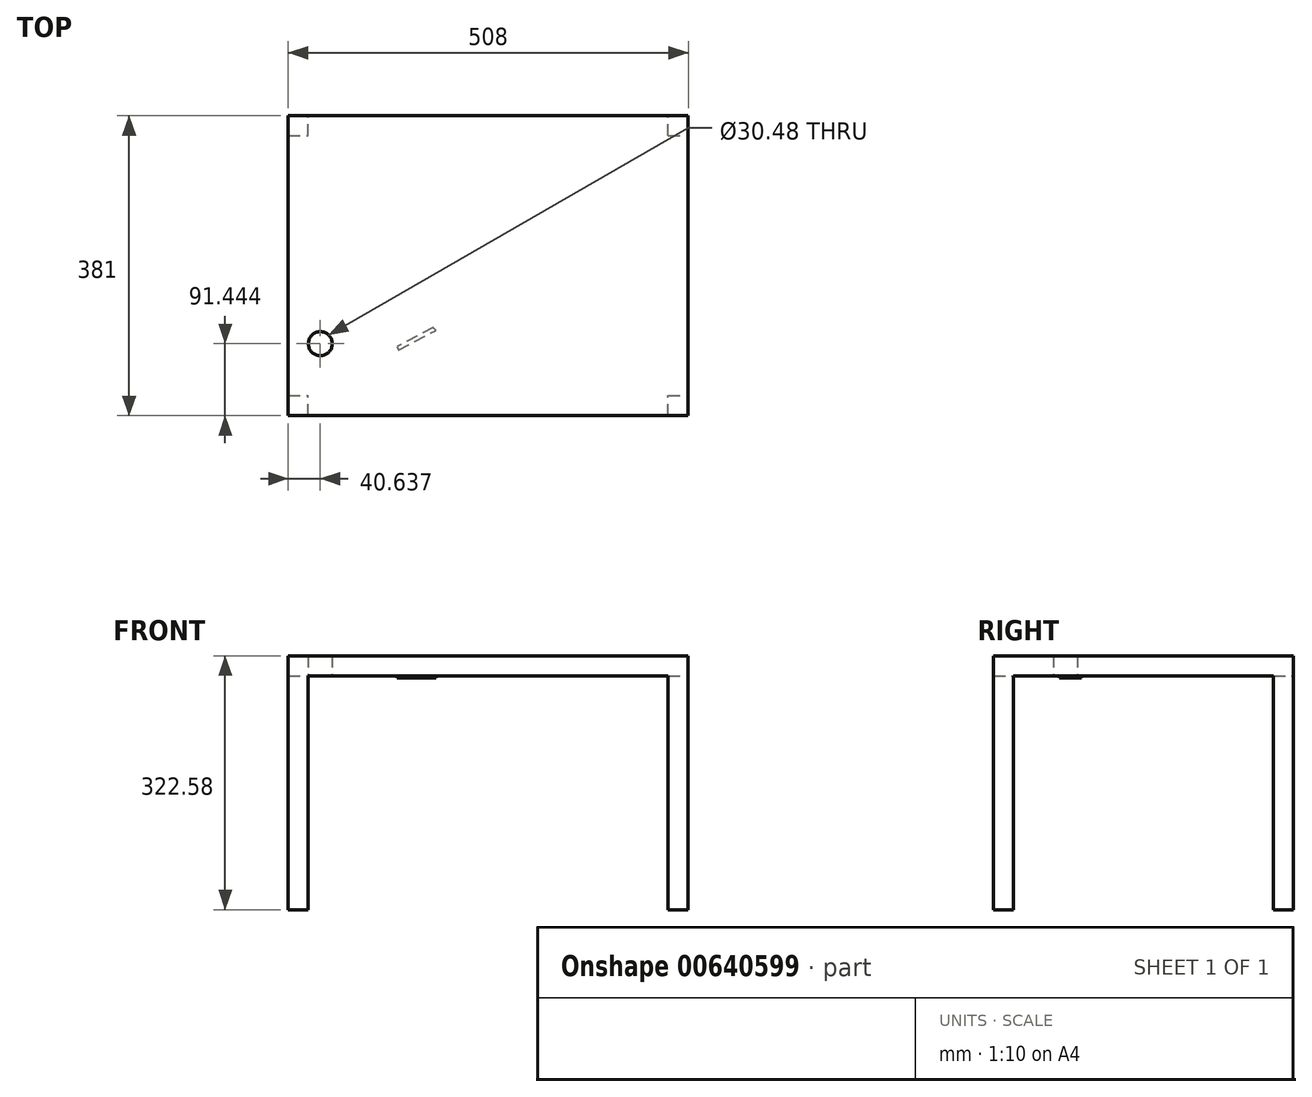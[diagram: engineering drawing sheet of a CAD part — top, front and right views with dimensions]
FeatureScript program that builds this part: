
annotation { "Feature Type Name" : "Feature", "Feature Type Description" : "" }
export const myFeature = defineFeature(function(context is Context, id is Id, definition is map)
    precondition{}
    {
        {
            var Q0;
            Q0=qCreatedBy(makeId("Top.planeOp"),FACE);
            var sketch = newSketch(context, id + "F0", { "sketchPlane" : qUnion([Q0])});
            skLineSegment(sketch, "E0.bottom", {"start": v(-266.43, 227.2) * mm, "end": v(241.57, 227.2) * mm});
            skLineSegment(sketch, "E0.top", {"start": v(-266.43, -153.8) * mm, "end": v(241.57, -153.8) * mm});
            skLineSegment(sketch, "E0.left", {"start": v(-266.43, 227.2) * mm, "end": v(-266.43, -153.8) * mm});
            skLineSegment(sketch, "E0.right", {"start": v(241.57, 227.2) * mm, "end": v(241.57, -153.8) * mm});
            skSolve(sketch);
        }
        {
            var Q0;
            Q0=makeQuery(id+"F0.imprint","IMPRINT",FACE,{"disambiguationData":[TD([[makeQuery(id+"F0.imprint","IMPRINT",EDGE,{"derivedFrom":sQuery(id+"F0.wireOp",EDGE,"E0.bottom")}),-1.0]])]});
            var sketch = newSketch(context, id + "F1", { "sketchPlane" : qUnion([Q0])});
            skSolve(sketch);
        }
        {
            var Q0;
            Q0=makeQuery(id+"F1.imprint","IMPRINT",FACE,{"disambiguationData":[TD([[makeQuery(id+"F1.imprint","IMPRINT",EDGE,{"derivedFrom":makeQuery(id+"F0.imprint","IMPRINT",EDGE,{"derivedFrom":sQuery(id+"F0.wireOp",EDGE,"E0.bottom")})}),-1.0]])]});
            var sketch = newSketch(context, id + "F2", { "sketchPlane" : qUnion([Q0])});
            skCircle(sketch, "E1", {"center": v(-225.8, -62.36) * mm, "radius": 15.24 * mm});
            skSolve(sketch);
        }
        {
            var Q0;
            Q0=makeQuery(id+"F2.imprint","IMPRINT",FACE,{"disambiguationData":[TD([[makeQuery(id+"F2.imprint","IMPRINT",EDGE,{"derivedFrom":sQuery(id+"F2.wireOp",EDGE,"E1")}),-1.0]])]});
            extrude(context, id + "F3", {"entities" : qUnion([Q0]), "depth" : 25.4 * mm, "offsetDistance" : 25.4 * mm});
        }
        {
            var Q0;
            Q0=makeQuery(id+"F0.imprint","IMPRINT",FACE,{"disambiguationData":[TD([[makeQuery(id+"F0.imprint","IMPRINT",EDGE,{"derivedFrom":sQuery(id+"F0.wireOp",EDGE,"E0.bottom")}),-1.0]])]});
            var sketch = newSketch(context, id + "F4", { "sketchPlane" : qUnion([Q0])});
            skLineSegment(sketch, "E2.bottom", {"start": v(-266.43, -153.8) * mm, "end": v(-241.03, -153.8) * mm});
            skLineSegment(sketch, "E2.top", {"start": v(-266.43, -128.4) * mm, "end": v(-241.03, -128.4) * mm});
            skLineSegment(sketch, "E2.left", {"start": v(-266.43, -153.8) * mm, "end": v(-266.43, -128.4) * mm});
            skLineSegment(sketch, "E2.right", {"start": v(-241.03, -153.8) * mm, "end": v(-241.03, -128.4) * mm});
            skLineSegment(sketch, "E3.bottom", {"start": v(-266.43, 201.8) * mm, "end": v(-241.03, 201.8) * mm});
            skLineSegment(sketch, "E3.top", {"start": v(-266.43, 227.2) * mm, "end": v(-241.03, 227.2) * mm});
            skLineSegment(sketch, "E3.left", {"start": v(-266.43, 201.8) * mm, "end": v(-266.43, 227.2) * mm});
            skLineSegment(sketch, "E3.right", {"start": v(-241.03, 201.8) * mm, "end": v(-241.03, 227.2) * mm});
            skLineSegment(sketch, "E4.bottom", {"start": v(216.17, -153.8) * mm, "end": v(241.57, -153.8) * mm});
            skLineSegment(sketch, "E4.top", {"start": v(216.17, -128.4) * mm, "end": v(241.57, -128.4) * mm});
            skLineSegment(sketch, "E4.left", {"start": v(216.17, -153.8) * mm, "end": v(216.17, -128.4) * mm});
            skLineSegment(sketch, "E4.right", {"start": v(241.57, -153.8) * mm, "end": v(241.57, -128.4) * mm});
            skLineSegment(sketch, "E5.bottom", {"start": v(216.17, 201.8) * mm, "end": v(241.57, 201.8) * mm});
            skLineSegment(sketch, "E5.top", {"start": v(216.17, 227.2) * mm, "end": v(241.57, 227.2) * mm});
            skLineSegment(sketch, "E5.left", {"start": v(216.17, 201.8) * mm, "end": v(216.17, 227.2) * mm});
            skLineSegment(sketch, "E5.right", {"start": v(241.57, 201.8) * mm, "end": v(241.57, 227.2) * mm});
            skSolve(sketch);
        }
        {
            var Q0;
            Q0=makeQuery(id+"F4.imprint","IMPRINT",FACE,{"disambiguationData":[TD([[makeQuery(id+"F4.imprint","IMPRINT",EDGE,{"derivedFrom":sQuery(id+"F4.wireOp",EDGE,"E2.bottom")}),1.0]])]});
            var Q1;
            Q1=makeQuery(id+"F4.imprint","IMPRINT",FACE,{"disambiguationData":[TD([[makeQuery(id+"F4.imprint","IMPRINT",EDGE,{"derivedFrom":sQuery(id+"F4.wireOp",EDGE,"E5.bottom")}),1.0]])]});
            var Q2;
            Q2=makeQuery(id+"F4.imprint","IMPRINT",FACE,{"disambiguationData":[TD([[makeQuery(id+"F4.imprint","IMPRINT",EDGE,{"derivedFrom":sQuery(id+"F4.wireOp",EDGE,"E4.bottom")}),1.0]])]});
            var Q3;
            Q3=makeQuery(id+"F4.imprint","IMPRINT",FACE,{"disambiguationData":[TD([[makeQuery(id+"F4.imprint","IMPRINT",EDGE,{"derivedFrom":sQuery(id+"F4.wireOp",EDGE,"E3.bottom")}),1.0]])]});
            extrude(context, id + "F5", {"entities" : qUnion([Q0, Q1, Q2, Q3]), "operationType" : NewBodyOperationType.ADD, "oppositeDirection" : true, "depth" : 297.18 * mm, "offsetDistance" : 25.4 * mm});
        }
        {
            var Q0;
            Q0=makeQuery(id+"F0.imprint","IMPRINT",FACE,{"disambiguationData":[TD([[makeQuery(id+"F0.imprint","IMPRINT",EDGE,{"derivedFrom":sQuery(id+"F0.wireOp",EDGE,"E0.bottom")}),-1.0]])]});
            var sketch = newSketch(context, id + "F6", { "sketchPlane" : qUnion([Q0])});
            skLineSegment(sketch, "E6", {"start": v(-82.64, -41.97) * mm, "end": v(-78.9, -45.39) * mm});
            skLineSegment(sketch, "E7", {"start": v(-82.64, -41.97) * mm, "end": v(-128.51, -65.78) * mm});
            skLineSegment(sketch, "E8", {"start": v(-128.51, -65.78) * mm, "end": v(-126.28, -70.08) * mm});
            skLineSegment(sketch, "E9", {"start": v(-126.28, -70.08) * mm, "end": v(-78.9, -45.39) * mm});
            skSolve(sketch);
        }
        {
            var Q0;
            Q0 = qSketchRegion(id + "F6", true);
            extrude(context, id + "F7", {"entities" : qUnion([Q0]), "operationType" : NewBodyOperationType.ADD, "oppositeDirection" : true, "depth" : 2.54 * mm, "offsetDistance" : 25.4 * mm});
        }
    });
